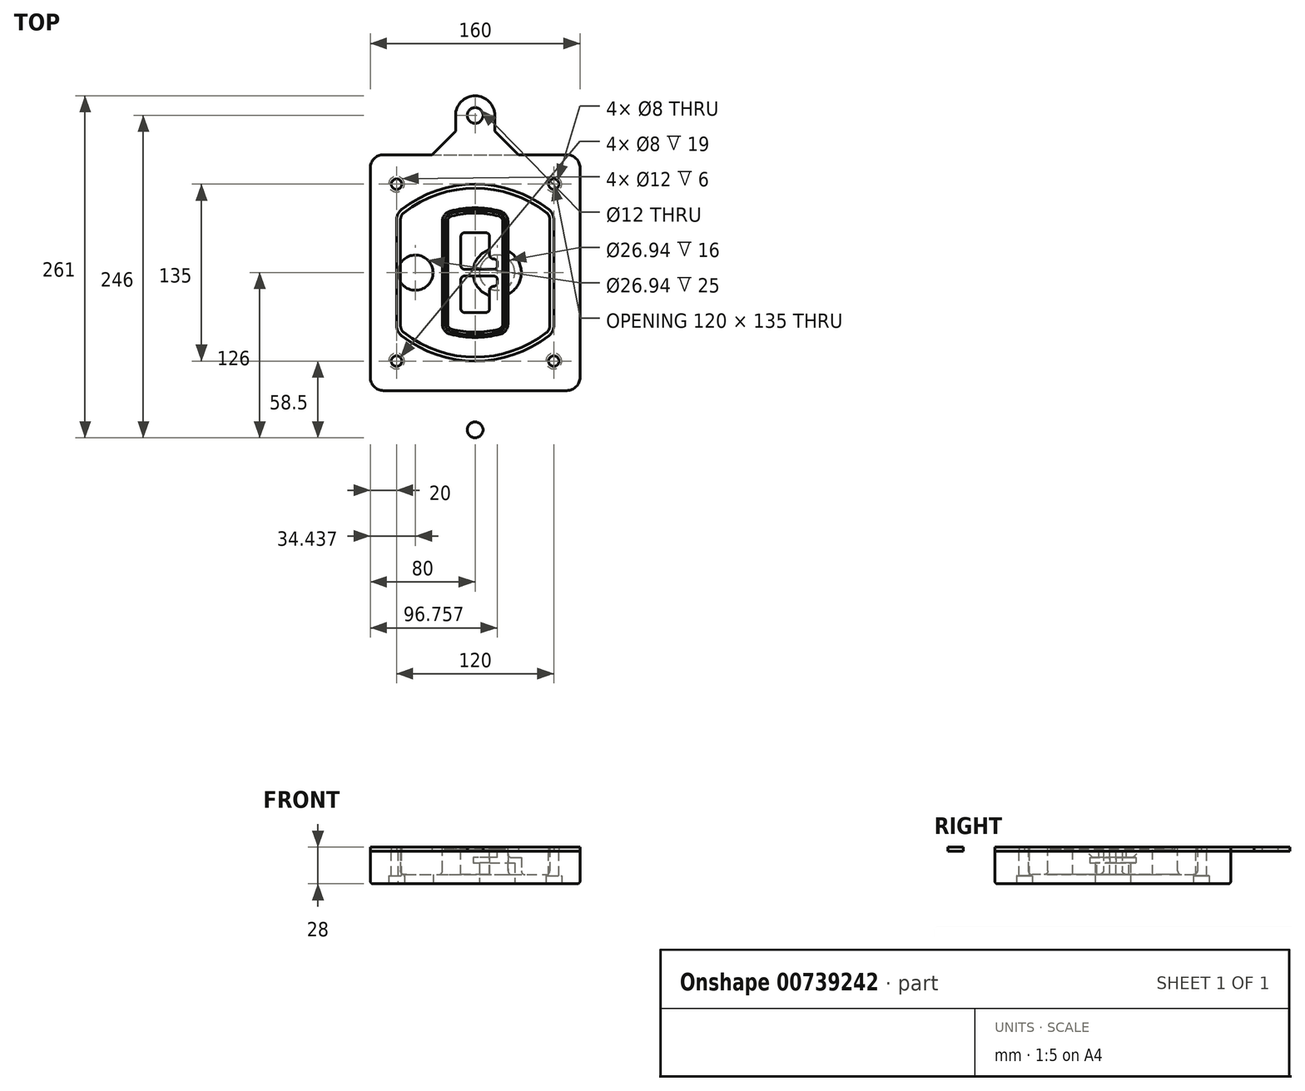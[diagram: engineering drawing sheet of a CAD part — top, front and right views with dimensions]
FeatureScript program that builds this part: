
annotation { "Feature Type Name" : "Feature", "Feature Type Description" : "" }
export const myFeature = defineFeature(function(context is Context, id is Id, definition is map)
    precondition{}
    {
        {
            var Q0;
            Q0=qCreatedBy(makeId("Top.planeOp"),FACE);
            var sketch = newSketch(context, id + "F0", { "sketchPlane" : qUnion([Q0])});
            skPoint(sketch, "E0.rect.middle", {"position": v(0, 0) * mm});
            skLineSegment(sketch, "E1.bottom", {"start": v(-70, -90) * mm, "end": v(70, -90) * mm});
            skLineSegment(sketch, "E1.top", {"start": v(-70, 90) * mm, "end": v(70, 90) * mm});
            skLineSegment(sketch, "E1.left", {"start": v(-80, -80) * mm, "end": v(-80, 80) * mm});
            skLineSegment(sketch, "E1.right", {"start": v(80, -80) * mm, "end": v(80, 80) * mm});
            skLineSegment(sketch, "E2", {"start": v(-80, 90) * mm, "end": v(80, -90) * mm, "construction": true});
            skLineSegment(sketch, "E3", {"start": v(80, 90) * mm, "end": v(-80, -90) * mm, "construction": true});
            skCircle(sketch, "E4", {"center": v(-60, 67.5) * mm, "radius": 4 * mm});
            skCircle(sketch, "E5", {"center": v(60, 67.5) * mm, "radius": 4 * mm});
            skCircle(sketch, "E6", {"center": v(60, -67.5) * mm, "radius": 4 * mm});
            skCircle(sketch, "E7", {"center": v(-60, -67.5) * mm, "radius": 4 * mm});
            skLineSegment(sketch, "E8", {"start": v(-60, 67.5) * mm, "end": v(60, 67.5) * mm, "construction": true});
            skLineSegment(sketch, "E9", {"start": v(60, 67.5) * mm, "end": v(60, -67.5) * mm, "construction": true});
            skLineSegment(sketch, "E10", {"start": v(60, -67.5) * mm, "end": v(-60, -67.5) * mm, "construction": true});
            skLineSegment(sketch, "E11", {"start": v(-60, -67.5) * mm, "end": v(-60, 67.5) * mm, "construction": true});
            skLineSegment(sketch, "E12", {"start": v(-60, 40.3) * mm, "end": v(-60, -40.3) * mm});
            skLineSegment(sketch, "E13", {"start": v(60, 40.3) * mm, "end": v(60, -40.3) * mm});
            skArc(sketch, "E14", {"start": v(56.15, 48.18) * mm, "mid": v(0, 67.5) * mm, "end": v(-56.15, 48.18) * mm});
            skArc(sketch, "E15", {"start": v(-56.15, -48.18) * mm, "mid": v(0, -67.5) * mm, "end": v(56.15, -48.18) * mm});
            skLineSegment(sketch, "E16", {"start": v(-60, 0) * mm, "end": v(60, 0) * mm, "construction": true});
            skPoint(sketch, "E17.visualSharp", {"position": v(-60, -45) * mm});
            skArc(sketch, "E17.filletArc", {"start": v(-60, -40.3) * mm, "mid": v(-58.99, -44.68) * mm, "end": v(-56.15, -48.18) * mm});
            skPoint(sketch, "E18.visualSharp", {"position": v(-60, 45) * mm});
            skArc(sketch, "E18.filletArc", {"start": v(-56.15, 48.18) * mm, "mid": v(-58.99, 44.68) * mm, "end": v(-60, 40.3) * mm});
            skPoint(sketch, "E19.visualSharp", {"position": v(60, 45) * mm});
            skArc(sketch, "E19.filletArc", {"start": v(60, 40.3) * mm, "mid": v(58.99, 44.68) * mm, "end": v(56.15, 48.18) * mm});
            skPoint(sketch, "E20.visualSharp", {"position": v(60, -45) * mm});
            skArc(sketch, "E20.filletArc", {"start": v(56.15, -48.18) * mm, "mid": v(58.99, -44.68) * mm, "end": v(60, -40.3) * mm});
            skPoint(sketch, "E21.visualSharp", {"position": v(-80, 90) * mm});
            skArc(sketch, "E21.filletArc", {"start": v(-70, 90) * mm, "mid": v(-77.07, 87.07) * mm, "end": v(-80, 80) * mm});
            skPoint(sketch, "E22.visualSharp", {"position": v(80, 90) * mm});
            skArc(sketch, "E22.filletArc", {"start": v(80, 80) * mm, "mid": v(77.07, 87.07) * mm, "end": v(70, 90) * mm});
            skPoint(sketch, "E23.visualSharp", {"position": v(80, -90) * mm});
            skArc(sketch, "E23.filletArc", {"start": v(70, -90) * mm, "mid": v(77.07, -87.07) * mm, "end": v(80, -80) * mm});
            skPoint(sketch, "E24.visualSharp", {"position": v(-80, -90) * mm});
            skArc(sketch, "E24.filletArc", {"start": v(-80, -80) * mm, "mid": v(-77.07, -87.07) * mm, "end": v(-70, -90) * mm});
            skArc(sketch, "E25.0", {"start": v(57, 40.3) * mm, "mid": v(56.3, 43.36) * mm, "end": v(54.3, 45.81) * mm});
            skLineSegment(sketch, "E25.1", {"start": v(57, 40.3) * mm, "end": v(57, -40.3) * mm});
            skArc(sketch, "E25.2", {"start": v(54.3, -45.81) * mm, "mid": v(56.3, -43.36) * mm, "end": v(57, -40.3) * mm});
            skArc(sketch, "E25.3", {"start": v(-54.3, -45.81) * mm, "mid": v(0, -64.5) * mm, "end": v(54.3, -45.81) * mm});
            skArc(sketch, "E25.4", {"start": v(-57, -40.3) * mm, "mid": v(-56.3, -43.36) * mm, "end": v(-54.3, -45.81) * mm});
            skArc(sketch, "E25.5", {"start": v(54.3, 45.81) * mm, "mid": v(0, 64.5) * mm, "end": v(-54.3, 45.81) * mm});
            skLineSegment(sketch, "E25.6", {"start": v(-57, 40.3) * mm, "end": v(-57, -40.3) * mm});
            skArc(sketch, "E25.7", {"start": v(-54.3, 45.81) * mm, "mid": v(-56.3, 43.36) * mm, "end": v(-57, 40.3) * mm});
            skArc(sketch, "E26.0", {"start": v(-58.62, 51.33) * mm, "mid": v(-62.58, 46.43) * mm, "end": v(-64, 40.3) * mm});
            skArc(sketch, "E26.1", {"start": v(58.62, 51.33) * mm, "mid": v(0, 71.5) * mm, "end": v(-58.62, 51.33) * mm});
            skArc(sketch, "E26.2", {"start": v(64, 40.3) * mm, "mid": v(62.58, 46.43) * mm, "end": v(58.62, 51.33) * mm});
            skLineSegment(sketch, "E26.3", {"start": v(64, 40.3) * mm, "end": v(64, -40.3) * mm});
            skArc(sketch, "E26.4", {"start": v(58.62, -51.33) * mm, "mid": v(62.58, -46.43) * mm, "end": v(64, -40.3) * mm});
            skLineSegment(sketch, "E26.5", {"start": v(-64, 40.3) * mm, "end": v(-64, -40.3) * mm});
            skArc(sketch, "E26.6", {"start": v(-58.62, -51.33) * mm, "mid": v(0, -71.5) * mm, "end": v(58.62, -51.33) * mm});
            skArc(sketch, "E26.7", {"start": v(-64, -40.3) * mm, "mid": v(-62.58, -46.43) * mm, "end": v(-58.62, -51.33) * mm});
            skSolve(sketch);
        }
        {
            var Q0;
            Q0=makeQuery(id+"F0.imprint","IMPRINT",FACE,{"disambiguationData":[TD([[makeQuery(id+"F0.imprint","IMPRINT",EDGE,{"derivedFrom":sQuery(id+"F0.wireOp",EDGE,"E1.bottom")}),1.0]])]});
            var Q1;
            Q1=makeQuery(id+"F0.imprint","IMPRINT",FACE,{"disambiguationData":[TD([[makeQuery(id+"F0.imprint","IMPRINT",EDGE,{"derivedFrom":sQuery(id+"F0.wireOp",EDGE,"E12")}),1.0]])]});
            var Q2;
            Q2=makeQuery(id+"F0.imprint","IMPRINT",FACE,{"disambiguationData":[TD([[makeQuery(id+"F0.imprint","IMPRINT",EDGE,{"derivedFrom":sQuery(id+"F0.wireOp",EDGE,"E25.0")}),1.0]])]});
            var Q3;
            Q3=makeQuery(id+"F0.imprint","IMPRINT",FACE,{"disambiguationData":[TD([[makeQuery(id+"F0.imprint","IMPRINT",EDGE,{"derivedFrom":sQuery(id+"F0.wireOp",EDGE,"E12")}),-1.0]])]});
            extrude(context, id + "F1", {"entities" : qUnion([Q0, Q1, Q2, Q3]), "oppositeDirection" : true, "depth" : 25 * mm});
        }
        {
            var Q0;
            Q0=makeQuery(id+"F0.imprint","IMPRINT",FACE,{"disambiguationData":[TD([[makeQuery(id+"F0.imprint","IMPRINT",EDGE,{"derivedFrom":sQuery(id+"F0.wireOp",EDGE,"E12")}),1.0]])]});
            extrude(context, id + "F2", {"entities" : qUnion([Q0]), "operationType" : NewBodyOperationType.ADD, "depth" : 3 * mm});
        }
        {
            var Q0;
            Q0=makeQuery(id+"F0.imprint","IMPRINT",FACE,{"disambiguationData":[TD([[makeQuery(id+"F0.imprint","IMPRINT",EDGE,{"derivedFrom":sQuery(id+"F0.wireOp",EDGE,"E25.0")}),1.0]])]});
            extrude(context, id + "F3", {"entities" : qUnion([Q0]), "operationType" : NewBodyOperationType.REMOVE, "oppositeDirection" : true, "depth" : 18 * mm});
        }
        {
            var Q0;
            Q0=makeQuery(id+"F2.opExtrude","CAP_FACE",FACE,{"disambiguationData":[OSD([sQuery(id+"F0.wireOp",EDGE,"E12"),sQuery(id+"F0.wireOp",EDGE,"E13"),sQuery(id+"F0.wireOp",EDGE,"E14"),sQuery(id+"F0.wireOp",EDGE,"E15"),sQuery(id+"F0.wireOp",EDGE,"E17.filletArc"),sQuery(id+"F0.wireOp",EDGE,"E18.filletArc"),sQuery(id+"F0.wireOp",EDGE,"E19.filletArc"),sQuery(id+"F0.wireOp",EDGE,"E20.filletArc"),sQuery(id+"F0.wireOp",EDGE,"E25.0"),sQuery(id+"F0.wireOp",EDGE,"E25.1"),sQuery(id+"F0.wireOp",EDGE,"E25.2"),sQuery(id+"F0.wireOp",EDGE,"E25.3"),sQuery(id+"F0.wireOp",EDGE,"E25.4"),sQuery(id+"F0.wireOp",EDGE,"E25.5"),sQuery(id+"F0.wireOp",EDGE,"E25.6"),sQuery(id+"F0.wireOp",EDGE,"E25.7")])],"isStart":false});
            var sketch = newSketch(context, id + "F4", { "sketchPlane" : qUnion([Q0])});
            skArc(sketch, "E27.0", {"start": v(-19.08, -46.97) * mm, "mid": v(0, -49.5) * mm, "end": v(19.08, -46.97) * mm});
            skArc(sketch, "E28.0", {"start": v(19.08, 46.97) * mm, "mid": v(0, 49.5) * mm, "end": v(-19.08, 46.97) * mm});
            skLineSegment(sketch, "E29", {"start": v(-25, 39.25) * mm, "end": v(-25, -39.25) * mm});
            skLineSegment(sketch, "E30", {"start": v(25, 39.25) * mm, "end": v(25, -39.25) * mm});
            skLineSegment(sketch, "E31", {"start": v(-25, 45.1) * mm, "end": v(25, 45.1) * mm, "construction": true});
            skLineSegment(sketch, "E32", {"start": v(-25, -45.1) * mm, "end": v(25, -45.1) * mm, "construction": true});
            skPoint(sketch, "E33.visualSharp", {"position": v(-25, 45.1) * mm});
            skArc(sketch, "E33.filletArc", {"start": v(-19.08, 46.97) * mm, "mid": v(-23.35, 44.11) * mm, "end": v(-25, 39.25) * mm});
            skPoint(sketch, "E34.visualSharp", {"position": v(25, 45.1) * mm});
            skArc(sketch, "E34.filletArc", {"start": v(25, 39.25) * mm, "mid": v(23.35, 44.11) * mm, "end": v(19.08, 46.97) * mm});
            skPoint(sketch, "E35.visualSharp", {"position": v(25, -45.1) * mm});
            skArc(sketch, "E35.filletArc", {"start": v(19.08, -46.97) * mm, "mid": v(23.35, -44.11) * mm, "end": v(25, -39.25) * mm});
            skPoint(sketch, "E36.visualSharp", {"position": v(-25, -45.1) * mm});
            skArc(sketch, "E36.filletArc", {"start": v(-25, -39.25) * mm, "mid": v(-23.35, -44.11) * mm, "end": v(-19.08, -46.97) * mm});
            skArc(sketch, "E37.0", {"start": v(54.3, 45.81) * mm, "mid": v(0, 64.5) * mm, "end": v(-54.3, 45.81) * mm});
            skArc(sketch, "E37.1", {"start": v(-54.3, 45.81) * mm, "mid": v(-56.3, 43.36) * mm, "end": v(-57, 40.3) * mm});
            skLineSegment(sketch, "E37.2", {"start": v(-57, 40.3) * mm, "end": v(-57, -40.3) * mm});
            skArc(sketch, "E37.3", {"start": v(-57, -40.3) * mm, "mid": v(-56.3, -43.36) * mm, "end": v(-54.3, -45.81) * mm});
            skArc(sketch, "E37.4", {"start": v(-54.3, -45.81) * mm, "mid": v(0, -64.5) * mm, "end": v(54.3, -45.81) * mm});
            skArc(sketch, "E37.5", {"start": v(54.3, -45.81) * mm, "mid": v(56.3, -43.36) * mm, "end": v(57, -40.3) * mm});
            skLineSegment(sketch, "E37.6", {"start": v(57, 40.3) * mm, "end": v(57, -40.3) * mm});
            skArc(sketch, "E37.7", {"start": v(57, 40.3) * mm, "mid": v(56.3, 43.36) * mm, "end": v(54.3, 45.81) * mm});
            skLineSegment(sketch, "E38.0", {"start": v(23, 39.25) * mm, "end": v(23, -39.25) * mm});
            skArc(sketch, "E38.1", {"start": v(18.56, -45.04) * mm, "mid": v(21.76, -42.9) * mm, "end": v(23, -39.25) * mm});
            skArc(sketch, "E38.2", {"start": v(-18.56, -45.04) * mm, "mid": v(0, -47.5) * mm, "end": v(18.56, -45.04) * mm});
            skArc(sketch, "E38.3", {"start": v(-23, -39.25) * mm, "mid": v(-21.76, -42.9) * mm, "end": v(-18.56, -45.04) * mm});
            skLineSegment(sketch, "E38.4", {"start": v(-23, 39.25) * mm, "end": v(-23, -39.25) * mm});
            skArc(sketch, "E38.5", {"start": v(23, 39.25) * mm, "mid": v(21.76, 42.9) * mm, "end": v(18.56, 45.04) * mm});
            skArc(sketch, "E38.6", {"start": v(-18.56, 45.04) * mm, "mid": v(-21.76, 42.9) * mm, "end": v(-23, 39.25) * mm});
            skArc(sketch, "E38.7", {"start": v(18.56, 45.04) * mm, "mid": v(0, 47.5) * mm, "end": v(-18.56, 45.04) * mm});
            skArc(sketch, "E39.0", {"start": v(21, 39.25) * mm, "mid": v(20.18, 41.68) * mm, "end": v(18.04, 43.1) * mm});
            skLineSegment(sketch, "E39.1", {"start": v(21, 39.25) * mm, "end": v(21, -39.25) * mm});
            skArc(sketch, "E39.2", {"start": v(18.04, -43.1) * mm, "mid": v(20.18, -41.68) * mm, "end": v(21, -39.25) * mm});
            skArc(sketch, "E39.3", {"start": v(-18.04, -43.1) * mm, "mid": v(0, -45.5) * mm, "end": v(18.04, -43.1) * mm});
            skArc(sketch, "E39.4", {"start": v(-21, -39.25) * mm, "mid": v(-20.18, -41.68) * mm, "end": v(-18.04, -43.1) * mm});
            skArc(sketch, "E39.5", {"start": v(18.04, 43.1) * mm, "mid": v(0, 45.5) * mm, "end": v(-18.04, 43.1) * mm});
            skLineSegment(sketch, "E39.6", {"start": v(-21, 39.25) * mm, "end": v(-21, -39.25) * mm});
            skArc(sketch, "E39.7", {"start": v(-18.04, 43.1) * mm, "mid": v(-20.18, 41.68) * mm, "end": v(-21, 39.25) * mm});
            skLineSegment(sketch, "E40", {"start": v(-25, 0) * mm, "end": v(25, 0) * mm, "construction": true});
            skLineSegment(sketch, "E41", {"start": v(-11, 5.5) * mm, "end": v(-11, 27.5) * mm});
            skLineSegment(sketch, "E42", {"start": v(-8, 30.5) * mm, "end": v(8, 30.5) * mm});
            skLineSegment(sketch, "E43", {"start": v(11, 27.5) * mm, "end": v(11, 13.5) * mm});
            skLineSegment(sketch, "E44", {"start": v(14, 10.5) * mm, "end": v(14, 10.5) * mm});
            skLineSegment(sketch, "E45", {"start": v(17, 7.5) * mm, "end": v(17, 5.5) * mm});
            skLineSegment(sketch, "E46", {"start": v(14, 2.5) * mm, "end": v(-8, 2.5) * mm});
            skPoint(sketch, "E47.visualSharp", {"position": v(-11, 30.5) * mm});
            skArc(sketch, "E47.filletArc", {"start": v(-8, 30.5) * mm, "mid": v(-10.12, 29.62) * mm, "end": v(-11, 27.5) * mm});
            skPoint(sketch, "E48.visualSharp", {"position": v(11, 30.5) * mm});
            skArc(sketch, "E48.filletArc", {"start": v(11, 27.5) * mm, "mid": v(10.12, 29.62) * mm, "end": v(8, 30.5) * mm});
            skPoint(sketch, "E49.visualSharp", {"position": v(11, 10.5) * mm});
            skArc(sketch, "E49.filletArc", {"start": v(11, 13.5) * mm, "mid": v(11.88, 11.38) * mm, "end": v(14, 10.5) * mm});
            skPoint(sketch, "E50.visualSharp", {"position": v(17, 10.5) * mm});
            skArc(sketch, "E50.filletArc", {"start": v(17, 7.5) * mm, "mid": v(16.12, 9.62) * mm, "end": v(14, 10.5) * mm});
            skPoint(sketch, "E51.visualSharp", {"position": v(17, 2.5) * mm});
            skArc(sketch, "E51.filletArc", {"start": v(14, 2.5) * mm, "mid": v(16.12, 3.38) * mm, "end": v(17, 5.5) * mm});
            skPoint(sketch, "E52.visualSharp", {"position": v(-11, 2.5) * mm});
            skArc(sketch, "E52.filletArc", {"start": v(-11, 5.5) * mm, "mid": v(-10.12, 3.38) * mm, "end": v(-8, 2.5) * mm});
            skLineSegment(sketch, "E53.0.MirrorCS", {"start": v(14, -2.5) * mm, "end": v(-8, -2.5) * mm});
            skArc(sketch, "E54.0.MirrorCS", {"start": v(-11, -5.5) * mm, "mid": v(-10.12, -3.38) * mm, "end": v(-8, -2.5) * mm});
            skLineSegment(sketch, "E55.0.MirrorCS", {"start": v(-11, -5.5) * mm, "end": v(-11, -27.5) * mm});
            skArc(sketch, "E56.0.MirrorCS", {"start": v(-8, -30.5) * mm, "mid": v(-10.12, -29.62) * mm, "end": v(-11, -27.5) * mm});
            skLineSegment(sketch, "E57.0.MirrorCS", {"start": v(-8, -30.5) * mm, "end": v(8, -30.5) * mm});
            skArc(sketch, "E58.0.MirrorCS", {"start": v(11, -27.5) * mm, "mid": v(10.12, -29.62) * mm, "end": v(8, -30.5) * mm});
            skLineSegment(sketch, "E59.0.MirrorCS", {"start": v(11, -27.5) * mm, "end": v(11, -13.5) * mm});
            skArc(sketch, "E60.0.MirrorCS", {"start": v(11, -13.5) * mm, "mid": v(11.88, -11.38) * mm, "end": v(14, -10.5) * mm});
            skArc(sketch, "E61.0.MirrorCS", {"start": v(17, -7.5) * mm, "mid": v(16.12, -9.62) * mm, "end": v(14, -10.5) * mm});
            skLineSegment(sketch, "E62.0.MirrorCS", {"start": v(17, -7.5) * mm, "end": v(17, -5.5) * mm});
            skArc(sketch, "E63.0.MirrorCS", {"start": v(14, -2.5) * mm, "mid": v(16.12, -3.38) * mm, "end": v(17, -5.5) * mm});
            skSolve(sketch);
        }
        {
            var Q0;
            Q0=makeQuery(id+"F4.imprint","IMPRINT",FACE,{"disambiguationData":[TD([[makeQuery(id+"F4.imprint","IMPRINT",EDGE,{"derivedFrom":sQuery(id+"F4.wireOp",EDGE,"E27.0")}),1.0]])]});
            var Q1;
            Q1=makeQuery(id+"F4.imprint","IMPRINT",FACE,{"disambiguationData":[TD([[makeQuery(id+"F4.imprint","IMPRINT",EDGE,{"derivedFrom":sQuery(id+"F4.wireOp",EDGE,"E38.0")}),-1.0]])]});
            var Q2;
            Q2=makeQuery(id+"F4.imprint","IMPRINT",FACE,{"disambiguationData":[TD([[makeQuery(id+"F4.imprint","IMPRINT",EDGE,{"derivedFrom":sQuery(id+"F4.wireOp",EDGE,"E39.0")}),1.0]])]});
            extrude(context, id + "F5", {"entities" : qUnion([Q0, Q1, Q2]), "operationType" : NewBodyOperationType.ADD, "endBound" : BoundingType.UP_TO_NEXT, "oppositeDirection" : true, "depth" : 25 * mm});
        }
        {
            var Q0;
            Q0=makeQuery(id+"F4.imprint","IMPRINT",FACE,{"disambiguationData":[TD([[makeQuery(id+"F4.imprint","IMPRINT",EDGE,{"derivedFrom":sQuery(id+"F4.wireOp",EDGE,"E38.0")}),-1.0]])]});
            extrude(context, id + "F6", {"entities" : qUnion([Q0]), "operationType" : NewBodyOperationType.REMOVE, "oppositeDirection" : true, "depth" : 2 * mm});
        }
        {
            var Q0;
            Q0=makeQuery(id+"F1.opExtrude","CAP_FACE",FACE,{"disambiguationData":[OSD([sQuery(id+"F0.wireOp",EDGE,"E1.bottom"),sQuery(id+"F0.wireOp",EDGE,"E1.top"),sQuery(id+"F0.wireOp",EDGE,"E1.left"),sQuery(id+"F0.wireOp",EDGE,"E1.right"),sQuery(id+"F0.wireOp",EDGE,"E4"),sQuery(id+"F0.wireOp",EDGE,"E5"),sQuery(id+"F0.wireOp",EDGE,"E6"),sQuery(id+"F0.wireOp",EDGE,"E7"),sQuery(id+"F0.wireOp",EDGE,"E21.filletArc"),sQuery(id+"F0.wireOp",EDGE,"E22.filletArc"),sQuery(id+"F0.wireOp",EDGE,"E23.filletArc"),sQuery(id+"F0.wireOp",EDGE,"E24.filletArc")])],"isStart":false});
            var sketch = newSketch(context, id + "F7", { "sketchPlane" : qUnion([Q0])});
            skCircle(sketch, "E64", {"center": v(16.76, 0) * mm, "radius": 13.47 * mm});
            skCircle(sketch, "E65", {"center": v(-45.56, 0) * mm, "radius": 13.47 * mm});
            skLineSegment(sketch, "E66", {"start": v(80, 0) * mm, "end": v(-80, 0) * mm});
            skCircle(sketch, "E67", {"center": v(16.76, 0) * mm, "radius": 18.47 * mm});
            skCircle(sketch, "E68", {"center": v(60, -67.5) * mm, "radius": 6 * mm});
            skCircle(sketch, "E69", {"center": v(-60, -67.5) * mm, "radius": 6 * mm});
            skCircle(sketch, "E70", {"center": v(-60, 67.5) * mm, "radius": 6 * mm});
            skCircle(sketch, "E71", {"center": v(60, 67.5) * mm, "radius": 6 * mm});
            skSolve(sketch);
        }
        {
            var Q0;
            {var subQ1=sQuery(id+"F7.wireOp",EDGE,"E66");var subQ4=sQuery(id+"F7.wireOp",EDGE,"E64");var subQ6=makeQuery(id+"F7.imprint","INTERSECT",VERTEX,{"disambiguationData":[OD(0.0)],"derivedFrom":[subQ4,subQ1]});Q0=makeQuery(id+"F7.imprint","IMPRINT",FACE,{"disambiguationData":[TD([[makeQuery(id+"F7.imprint","IMPRINT",EDGE,{"disambiguationData":[TD([[subQ6,-1.0]])],"derivedFrom":subQ4}),-1.0]])]});}
            var Q1;
            {var subQ0=sQuery(id+"F7.wireOp",EDGE,"E66");var subQ1=sQuery(id+"F7.wireOp",EDGE,"E64");var subQ3=makeQuery(id+"F7.imprint","INTERSECT",VERTEX,{"disambiguationData":[OD(0.0)],"derivedFrom":[subQ1,subQ0]});Q1=makeQuery(id+"F7.imprint","IMPRINT",FACE,{"disambiguationData":[TD([[makeQuery(id+"F7.imprint","IMPRINT",EDGE,{"disambiguationData":[TD([[subQ3,-1.0]])],"derivedFrom":subQ1}),1.0]])]});}
            var Q2;
            {var subQ0=sQuery(id+"F7.wireOp",EDGE,"E66");var subQ1=sQuery(id+"F7.wireOp",EDGE,"E64");var subQ3=makeQuery(id+"F7.imprint","INTERSECT",VERTEX,{"disambiguationData":[OD(0.0)],"derivedFrom":[subQ1,subQ0]});Q2=makeQuery(id+"F7.imprint","IMPRINT",FACE,{"disambiguationData":[TD([[makeQuery(id+"F7.imprint","IMPRINT",EDGE,{"disambiguationData":[TD([[subQ3,1.0]])],"derivedFrom":subQ1}),1.0]])]});}
            var Q3;
            {var subQ1=sQuery(id+"F7.wireOp",EDGE,"E66");var subQ4=sQuery(id+"F7.wireOp",EDGE,"E64");var subQ6=makeQuery(id+"F7.imprint","INTERSECT",VERTEX,{"disambiguationData":[OD(0.0)],"derivedFrom":[subQ4,subQ1]});Q3=makeQuery(id+"F7.imprint","IMPRINT",FACE,{"disambiguationData":[TD([[makeQuery(id+"F7.imprint","IMPRINT",EDGE,{"disambiguationData":[TD([[subQ6,1.0]])],"derivedFrom":subQ4}),-1.0]])]});}
            extrude(context, id + "F8", {"entities" : qUnion([Q0, Q1, Q2, Q3]), "operationType" : NewBodyOperationType.ADD, "oppositeDirection" : true, "depth" : 20 * mm});
        }
        {
            var Q0;
            {var subQ0=sQuery(id+"F7.wireOp",EDGE,"E66");var subQ1=sQuery(id+"F7.wireOp",EDGE,"E64");var subQ3=makeQuery(id+"F7.imprint","INTERSECT",VERTEX,{"disambiguationData":[OD(0.0)],"derivedFrom":[subQ1,subQ0]});Q0=makeQuery(id+"F7.imprint","IMPRINT",FACE,{"disambiguationData":[TD([[makeQuery(id+"F7.imprint","IMPRINT",EDGE,{"disambiguationData":[TD([[subQ3,-1.0]])],"derivedFrom":subQ1}),1.0]])]});}
            var Q1;
            {var subQ0=sQuery(id+"F7.wireOp",EDGE,"E66");var subQ1=sQuery(id+"F7.wireOp",EDGE,"E64");var subQ3=makeQuery(id+"F7.imprint","INTERSECT",VERTEX,{"disambiguationData":[OD(0.0)],"derivedFrom":[subQ1,subQ0]});Q1=makeQuery(id+"F7.imprint","IMPRINT",FACE,{"disambiguationData":[TD([[makeQuery(id+"F7.imprint","IMPRINT",EDGE,{"disambiguationData":[TD([[subQ3,1.0]])],"derivedFrom":subQ1}),1.0]])]});}
            extrude(context, id + "F9", {"entities" : qUnion([Q0, Q1]), "operationType" : NewBodyOperationType.REMOVE, "oppositeDirection" : true, "depth" : 16 * mm});
        }
        {
            var Q0;
            {var subQ0=sQuery(id+"F7.wireOp",EDGE,"E66");var subQ1=sQuery(id+"F7.wireOp",EDGE,"E65");var subQ3=makeQuery(id+"F7.imprint","INTERSECT",VERTEX,{"disambiguationData":[OD(0.0)],"derivedFrom":[subQ1,subQ0]});Q0=makeQuery(id+"F7.imprint","IMPRINT",FACE,{"disambiguationData":[TD([[makeQuery(id+"F7.imprint","IMPRINT",EDGE,{"disambiguationData":[TD([[subQ3,-1.0]])],"derivedFrom":subQ1}),1.0]])]});}
            var Q1;
            {var subQ0=sQuery(id+"F7.wireOp",EDGE,"E66");var subQ1=sQuery(id+"F7.wireOp",EDGE,"E65");var subQ3=makeQuery(id+"F7.imprint","INTERSECT",VERTEX,{"disambiguationData":[OD(0.0)],"derivedFrom":[subQ1,subQ0]});Q1=makeQuery(id+"F7.imprint","IMPRINT",FACE,{"disambiguationData":[TD([[makeQuery(id+"F7.imprint","IMPRINT",EDGE,{"disambiguationData":[TD([[subQ3,1.0]])],"derivedFrom":subQ1}),1.0]])]});}
            extrude(context, id + "F10", {"entities" : qUnion([Q0, Q1]), "operationType" : NewBodyOperationType.REMOVE, "oppositeDirection" : true, "depth" : 25 * mm});
        }
        {
            var Q0;
            Q0=makeQuery(id+"F7.imprint","IMPRINT",FACE,{"disambiguationData":[TD([[makeQuery(id+"F7.imprint","IMPRINT",EDGE,{"derivedFrom":sQuery(id+"F7.wireOp",EDGE,"E68")}),1.0]])]});
            var Q1;
            Q1=makeQuery(id+"F7.imprint","IMPRINT",FACE,{"disambiguationData":[TD([[makeQuery(id+"F7.imprint","IMPRINT",EDGE,{"derivedFrom":makeQuery(id+"F1.opExtrude","CAP_EDGE",EDGE,{"disambiguationData":[OSD([sQuery(id+"F0.wireOp",EDGE,"E5")])],"isStart":false})}),-1.0]])]});
            var Q2;
            Q2=makeQuery(id+"F7.imprint","IMPRINT",FACE,{"disambiguationData":[TD([[makeQuery(id+"F7.imprint","IMPRINT",EDGE,{"derivedFrom":sQuery(id+"F7.wireOp",EDGE,"E69")}),1.0]])]});
            var Q3;
            Q3=makeQuery(id+"F7.imprint","IMPRINT",FACE,{"disambiguationData":[TD([[makeQuery(id+"F7.imprint","IMPRINT",EDGE,{"derivedFrom":makeQuery(id+"F1.opExtrude","CAP_EDGE",EDGE,{"disambiguationData":[OSD([sQuery(id+"F0.wireOp",EDGE,"E4")])],"isStart":false})}),-1.0]])]});
            var Q4;
            Q4=makeQuery(id+"F7.imprint","IMPRINT",FACE,{"disambiguationData":[TD([[makeQuery(id+"F7.imprint","IMPRINT",EDGE,{"derivedFrom":sQuery(id+"F7.wireOp",EDGE,"E70")}),1.0]])]});
            var Q5;
            Q5=makeQuery(id+"F7.imprint","IMPRINT",FACE,{"disambiguationData":[TD([[makeQuery(id+"F7.imprint","IMPRINT",EDGE,{"derivedFrom":makeQuery(id+"F1.opExtrude","CAP_EDGE",EDGE,{"disambiguationData":[OSD([sQuery(id+"F0.wireOp",EDGE,"E7")])],"isStart":false})}),-1.0]])]});
            var Q6;
            Q6=makeQuery(id+"F7.imprint","IMPRINT",FACE,{"disambiguationData":[TD([[makeQuery(id+"F7.imprint","IMPRINT",EDGE,{"derivedFrom":sQuery(id+"F7.wireOp",EDGE,"E71")}),1.0]])]});
            var Q7;
            Q7=makeQuery(id+"F7.imprint","IMPRINT",FACE,{"disambiguationData":[TD([[makeQuery(id+"F7.imprint","IMPRINT",EDGE,{"derivedFrom":makeQuery(id+"F1.opExtrude","CAP_EDGE",EDGE,{"disambiguationData":[OSD([sQuery(id+"F0.wireOp",EDGE,"E6")])],"isStart":false})}),-1.0]])]});
            extrude(context, id + "F11", {"entities" : qUnion([Q0, Q1, Q2, Q3, Q4, Q5, Q6, Q7]), "operationType" : NewBodyOperationType.REMOVE, "oppositeDirection" : true, "depth" : 6 * mm});
        }
        {
            var Q0;
            Q0=makeQuery(id+"F9.boolean.opBoolean","COPY",FACE,{"derivedFrom":makeQuery(id+"F9.opExtrude","CAP_FACE",FACE,{"disambiguationData":[OSD([sQuery(id+"F7.wireOp",EDGE,"E64")])],"isStart":false})});
            var sketch = newSketch(context, id + "F12", { "sketchPlane" : qUnion([Q0])});
            skArc(sketch, "E72.0", {"start": v(11, 17.55) * mm, "mid": v(2.57, 11.82) * mm, "end": v(-1.54, 2.5) * mm});
            skArc(sketch, "E72.1", {"start": v(-1.54, -2.5) * mm, "mid": v(2.57, -11.82) * mm, "end": v(11, -17.55) * mm});
            skLineSegment(sketch, "E73", {"start": v(-1.54, -2.5) * mm, "end": v(14, -2.5) * mm});
            skLineSegment(sketch, "E74.0", {"start": v(14, 2.5) * mm, "end": v(-1.54, 2.5) * mm});
            skArc(sketch, "E74.1", {"start": v(14, 2.5) * mm, "mid": v(16.12, 3.38) * mm, "end": v(17, 5.5) * mm});
            skLineSegment(sketch, "E74.2", {"start": v(17, 7.5) * mm, "end": v(17, 5.5) * mm});
            skArc(sketch, "E74.3", {"start": v(17, 7.5) * mm, "mid": v(16.12, 9.62) * mm, "end": v(14, 10.5) * mm});
            skArc(sketch, "E74.4", {"start": v(11, 13.5) * mm, "mid": v(11.88, 11.38) * mm, "end": v(14, 10.5) * mm});
            skLineSegment(sketch, "E74.5", {"start": v(11, 17.55) * mm, "end": v(11, 13.5) * mm});
            skLineSegment(sketch, "E74.7", {"start": v(14, -2.5) * mm, "end": v(-1.54, -2.5) * mm});
            skArc(sketch, "E74.8", {"start": v(14, -2.5) * mm, "mid": v(16.12, -3.38) * mm, "end": v(17, -5.5) * mm});
            skLineSegment(sketch, "E74.9", {"start": v(17, -7.5) * mm, "end": v(17, -5.5) * mm});
            skArc(sketch, "E74.10", {"start": v(17, -7.5) * mm, "mid": v(16.12, -9.62) * mm, "end": v(14, -10.5) * mm});
            skArc(sketch, "E74.11", {"start": v(11, -13.5) * mm, "mid": v(11.88, -11.38) * mm, "end": v(14, -10.5) * mm});
            skLineSegment(sketch, "E74.12", {"start": v(11, -17.55) * mm, "end": v(11, -13.5) * mm});
            skPoint(sketch, "E75.orphan", {"position": v(11, -27.5) * mm});
            skPoint(sketch, "E76.orphan", {"position": v(-8, -2.5) * mm});
            skPoint(sketch, "E77.orphan", {"position": v(-8, 2.5) * mm});
            skPoint(sketch, "E78.orphan", {"position": v(11, 27.5) * mm});
            skSolve(sketch);
        }
        {
            var Q0;
            {var subQ7=sQuery(id+"F12.wireOp",EDGE,"E72.0");var subQ14=sQuery(id+"F12.wireOp",EDGE,"E72.1");var subQ16=sQuery(id+"F12.wireOp",EDGE,"E74.1");var subQ18=sQuery(id+"F12.wireOp",EDGE,"E74.8");Q0=qUnion([makeQuery(id+"F12.imprint","IMPRINT",FACE,{"disambiguationData":[TD([[makeQuery(id+"F12.imprint","IMPRINT",EDGE,{"derivedFrom":subQ7}),1.0]])]}),makeQuery(id+"F12.imprint","IMPRINT",FACE,{"disambiguationData":[TD([[makeQuery(id+"F12.imprint","IMPRINT",EDGE,{"derivedFrom":subQ14}),1.0]])]}),makeQuery(id+"F12.imprint","IMPRINT",FACE,{"disambiguationData":[TD([[makeQuery(id+"F12.imprint","IMPRINT",EDGE,{"derivedFrom":subQ16}),1.0]])]}),makeQuery(id+"F12.imprint","IMPRINT",FACE,{"disambiguationData":[TD([[makeQuery(id+"F12.imprint","IMPRINT",EDGE,{"derivedFrom":subQ18}),-1.0]])]})]);}
            var Q1;
            Q1=makeQuery(id+"F5.boolean.opBoolean","SPLIT",FACE,{"disambiguationData":[TD([makeQuery(id+"F5.opExtrude","SWEPT_FACE",FACE,{"disambiguationData":[OSD([sQuery(id+"F4.wireOp",EDGE,"E41")])]})])],"derivedFrom":makeQuery(id+"F3.boolean.opBoolean","COPY",FACE,{"derivedFrom":makeQuery(id+"F3.opExtrude","CAP_FACE",FACE,{"disambiguationData":[OSD([sQuery(id+"F0.wireOp",EDGE,"E25.0"),sQuery(id+"F0.wireOp",EDGE,"E25.1"),sQuery(id+"F0.wireOp",EDGE,"E25.2"),sQuery(id+"F0.wireOp",EDGE,"E25.3"),sQuery(id+"F0.wireOp",EDGE,"E25.4"),sQuery(id+"F0.wireOp",EDGE,"E25.5"),sQuery(id+"F0.wireOp",EDGE,"E25.6"),sQuery(id+"F0.wireOp",EDGE,"E25.7")])],"isStart":false})})});
            extrude(context, id + "F13", {"entities" : qUnion([Q0]), "operationType" : NewBodyOperationType.REMOVE, "endBound" : BoundingType.UP_TO_SURFACE, "endBoundEntityFace" : qUnion([Q1]), "depth" : 25 * mm});
        }
        {
            var Q0;
            Q0=makeQuery(id+"F3.boolean.opBoolean","COPY",EDGE,{"derivedFrom":makeQuery(id+"F3.opExtrude","CAP_EDGE",EDGE,{"disambiguationData":[OSD([sQuery(id+"F0.wireOp",EDGE,"E25.6")])],"isStart":false})});
            var Q1;
            Q1=makeQuery(id+"F8.boolean.opBoolean","INTERSECT",EDGE,{"derivedFrom":[makeQuery(id+"F5.opExtrude","SWEPT_FACE",FACE,{"disambiguationData":[OSD([sQuery(id+"F4.wireOp",EDGE,"E30")])]}),makeQuery(id+"F8.opExtrude","CAP_FACE",FACE,{"disambiguationData":[OSD([sQuery(id+"F7.wireOp",EDGE,"E67")])],"isStart":false})]});
            var Q2;
            Q2=makeQuery(id+"F8.boolean.opBoolean","INTERSECT",EDGE,{"disambiguationData":[OD(1.0)],"derivedFrom":[makeQuery(id+"F5.opExtrude","SWEPT_FACE",FACE,{"disambiguationData":[OSD([sQuery(id+"F4.wireOp",EDGE,"E30")])]}),makeQuery(id+"F8.opExtrude","SWEPT_FACE",FACE,{"disambiguationData":[OSD([sQuery(id+"F7.wireOp",EDGE,"E67")])]})]});
            var Q3;
            {var subQ0=sQuery(id+"F4.wireOp",EDGE,"E30");Q3=makeQuery(id+"F8.boolean.opBoolean","SPLIT",EDGE,{"disambiguationData":[TD([makeQuery(id+"F5.opExtrude","SWEPT_FACE",FACE,{"disambiguationData":[OSD([sQuery(id+"F4.wireOp",EDGE,"E35.filletArc")])]})])],"derivedFrom":makeQuery(id+"F5.opExtrude","CAP_EDGE",EDGE,{"disambiguationData":[OSD([subQ0])],"isStart":false})});}
            var Q4;
            {var subQ0=sQuery(id+"F0.wireOp",EDGE,"E25.7");var subQ1=sQuery(id+"F0.wireOp",EDGE,"E25.1");var subQ2=sQuery(id+"F0.wireOp",EDGE,"E25.6");var subQ3=sQuery(id+"F0.wireOp",EDGE,"E25.5");var subQ4=sQuery(id+"F0.wireOp",EDGE,"E25.4");var subQ5=sQuery(id+"F0.wireOp",EDGE,"E25.0");var subQ6=sQuery(id+"F0.wireOp",EDGE,"E25.2");var subQ7=sQuery(id+"F0.wireOp",EDGE,"E25.3");Q4=makeQuery(id+"F8.boolean.opBoolean","INTERSECT",EDGE,{"derivedFrom":[makeQuery(id+"F5.boolean.opBoolean","SPLIT",FACE,{"disambiguationData":[TD([makeQuery(id+"F2.opExtrude","SWEPT_FACE",FACE,{"disambiguationData":[OSD([subQ5])]})])],"derivedFrom":makeQuery(id+"F3.boolean.opBoolean","COPY",FACE,{"derivedFrom":makeQuery(id+"F3.opExtrude","CAP_FACE",FACE,{"disambiguationData":[OSD([subQ5,subQ1,subQ6,subQ7,subQ4,subQ3,subQ2,subQ0])],"isStart":false})})}),makeQuery(id+"F8.opExtrude","SWEPT_FACE",FACE,{"disambiguationData":[OSD([sQuery(id+"F7.wireOp",EDGE,"E67")])]})]});}
            var Q5;
            Q5=makeQuery(id+"F8.boolean.opBoolean","INTERSECT",EDGE,{"disambiguationData":[OD(0.0)],"derivedFrom":[makeQuery(id+"F5.opExtrude","SWEPT_FACE",FACE,{"disambiguationData":[OSD([sQuery(id+"F4.wireOp",EDGE,"E30")])]}),makeQuery(id+"F8.opExtrude","SWEPT_FACE",FACE,{"disambiguationData":[OSD([sQuery(id+"F7.wireOp",EDGE,"E67")])]})]});
            fillet(context, id + "F14", {"entities" : qUnion([Q0, Q1, Q2, Q3, Q4, Q5]), "radius" : 3 * mm, "tangentPropagation" : true, "allowEdgeOverflow" : false});
        }
        {
            var Q0;
            Q0=makeQuery(id+"F1.opExtrude","CAP_EDGE",EDGE,{"disambiguationData":[OSD([sQuery(id+"F0.wireOp",EDGE,"E1.bottom")])],"isStart":false});
            fillet(context, id + "F15", {"entities" : qUnion([Q0]), "radius" : 2 * mm, "tangentPropagation" : true, "allowEdgeOverflow" : false});
        }
        {
            var Q0;
            {var subQ0=sQuery(id+"F0.wireOp",EDGE,"E21.filletArc");var subQ1=sQuery(id+"F0.wireOp",EDGE,"E7");var subQ2=sQuery(id+"F0.wireOp",EDGE,"E6");var subQ3=sQuery(id+"F0.wireOp",EDGE,"E5");var subQ4=sQuery(id+"F0.wireOp",EDGE,"E4");var subQ5=sQuery(id+"F0.wireOp",EDGE,"E22.filletArc");var subQ6=sQuery(id+"F0.wireOp",EDGE,"E1.bottom");var subQ7=sQuery(id+"F0.wireOp",EDGE,"E1.right");var subQ8=sQuery(id+"F0.wireOp",EDGE,"E1.top");var subQ9=sQuery(id+"F0.wireOp",EDGE,"E1.left");var subQ10=sQuery(id+"F0.wireOp",EDGE,"E23.filletArc");var subQ11=sQuery(id+"F0.wireOp",EDGE,"E24.filletArc");Q0=makeQuery(id+"F2.boolean.opBoolean","SPLIT",FACE,{"disambiguationData":[TD([makeQuery(id+"F1.opExtrude","SWEPT_FACE",FACE,{"disambiguationData":[OSD([subQ6])]})])],"derivedFrom":makeQuery(id+"F1.opExtrude","CAP_FACE",FACE,{"disambiguationData":[OSD([subQ6,subQ8,subQ9,subQ7,subQ4,subQ3,subQ2,subQ1,subQ0,subQ5,subQ10,subQ11])],"isStart":true})});}
            var sketch = newSketch(context, id + "F16", { "sketchPlane" : qUnion([Q0])});
            skLineSegment(sketch, "E79", {"start": v(-74.8, 0) * mm, "end": v(74.47, 0) * mm, "construction": true});
            skLineSegment(sketch, "E80", {"start": v(0, 90) * mm, "end": v(0, 120) * mm, "construction": true});
            skCircle(sketch, "E81", {"center": v(0, 120) * mm, "radius": 6 * mm});
            skLineSegment(sketch, "E82", {"start": v(-33, 90) * mm, "end": v(-15, 108) * mm});
            skLineSegment(sketch, "E83", {"start": v(-15, 108) * mm, "end": v(-15, 120) * mm});
            skLineSegment(sketch, "E84", {"start": v(33, 90) * mm, "end": v(15, 108) * mm});
            skLineSegment(sketch, "E85", {"start": v(15, 108) * mm, "end": v(15, 120) * mm});
            skArc(sketch, "E86", {"start": v(15, 120) * mm, "mid": v(0, 135) * mm, "end": v(-15, 120) * mm});
            skLineSegment(sketch, "E87.MirrorCS", {"start": v(-33, -90) * mm, "end": v(-15, -108) * mm});
            skLineSegment(sketch, "E88.MirrorCS", {"start": v(33, -90) * mm, "end": v(15, -108) * mm});
            skLineSegment(sketch, "E89.MirrorCS", {"start": v(0, -90) * mm, "end": v(0, -120) * mm, "construction": true});
            skCircle(sketch, "E90.MirrorC", {"center": v(0, -120) * mm, "radius": 6 * mm});
            skLineSegment(sketch, "E91.MirrorCS", {"start": v(15, -108) * mm, "end": v(15, -120) * mm});
            skArc(sketch, "E92.MirrorCS", {"start": v(15, -120) * mm, "mid": v(0, -135) * mm, "end": v(-15, -120) * mm});
            skLineSegment(sketch, "E93.MirrorCS", {"start": v(-15, -108) * mm, "end": v(-15, -120) * mm});
            skSolve(sketch);
        }
        {
            var Q0;
            Q0=makeQuery(id+"F16.imprint","IMPRINT",FACE,{"disambiguationData":[TD([[makeQuery(id+"F16.imprint","IMPRINT",EDGE,{"derivedFrom":sQuery(id+"F16.wireOp",EDGE,"E90.MirrorC")}),1.0]])]});
            var Q1;
            Q1=makeQuery(id+"F16.imprint","IMPRINT",FACE,{"disambiguationData":[TD([[makeQuery(id+"F16.imprint","IMPRINT",EDGE,{"derivedFrom":sQuery(id+"F16.wireOp",EDGE,"E81")}),-1.0]])]});
            var Q2;
            Q2=makeQuery(id+"F16.imprint","IMPRINT",FACE,{"disambiguationData":[TD([[makeQuery(id+"F16.imprint","IMPRINT",EDGE,{"derivedFrom":makeQuery(id+"F1.opExtrude","CAP_EDGE",EDGE,{"disambiguationData":[OSD([sQuery(id+"F0.wireOp",EDGE,"E1.left")])],"isStart":true})}),-1.0]])]});
            var Q3;
            Q3=makeQuery(id+"F2.opExtrude","CAP_FACE",FACE,{"disambiguationData":[OSD([sQuery(id+"F0.wireOp",EDGE,"E12"),sQuery(id+"F0.wireOp",EDGE,"E13"),sQuery(id+"F0.wireOp",EDGE,"E14"),sQuery(id+"F0.wireOp",EDGE,"E15"),sQuery(id+"F0.wireOp",EDGE,"E17.filletArc"),sQuery(id+"F0.wireOp",EDGE,"E18.filletArc"),sQuery(id+"F0.wireOp",EDGE,"E19.filletArc"),sQuery(id+"F0.wireOp",EDGE,"E20.filletArc"),sQuery(id+"F0.wireOp",EDGE,"E25.0"),sQuery(id+"F0.wireOp",EDGE,"E25.1"),sQuery(id+"F0.wireOp",EDGE,"E25.2"),sQuery(id+"F0.wireOp",EDGE,"E25.3"),sQuery(id+"F0.wireOp",EDGE,"E25.4"),sQuery(id+"F0.wireOp",EDGE,"E25.5"),sQuery(id+"F0.wireOp",EDGE,"E25.6"),sQuery(id+"F0.wireOp",EDGE,"E25.7")])],"isStart":false});
            extrude(context, id + "F17", {"entities" : qUnion([Q0, Q1, Q2]), "endBound" : BoundingType.UP_TO_SURFACE, "depth" : 25 * mm, "endBoundEntityFace" : qUnion([Q3]), "offsetDistance" : 25 * mm});
        }
    });
